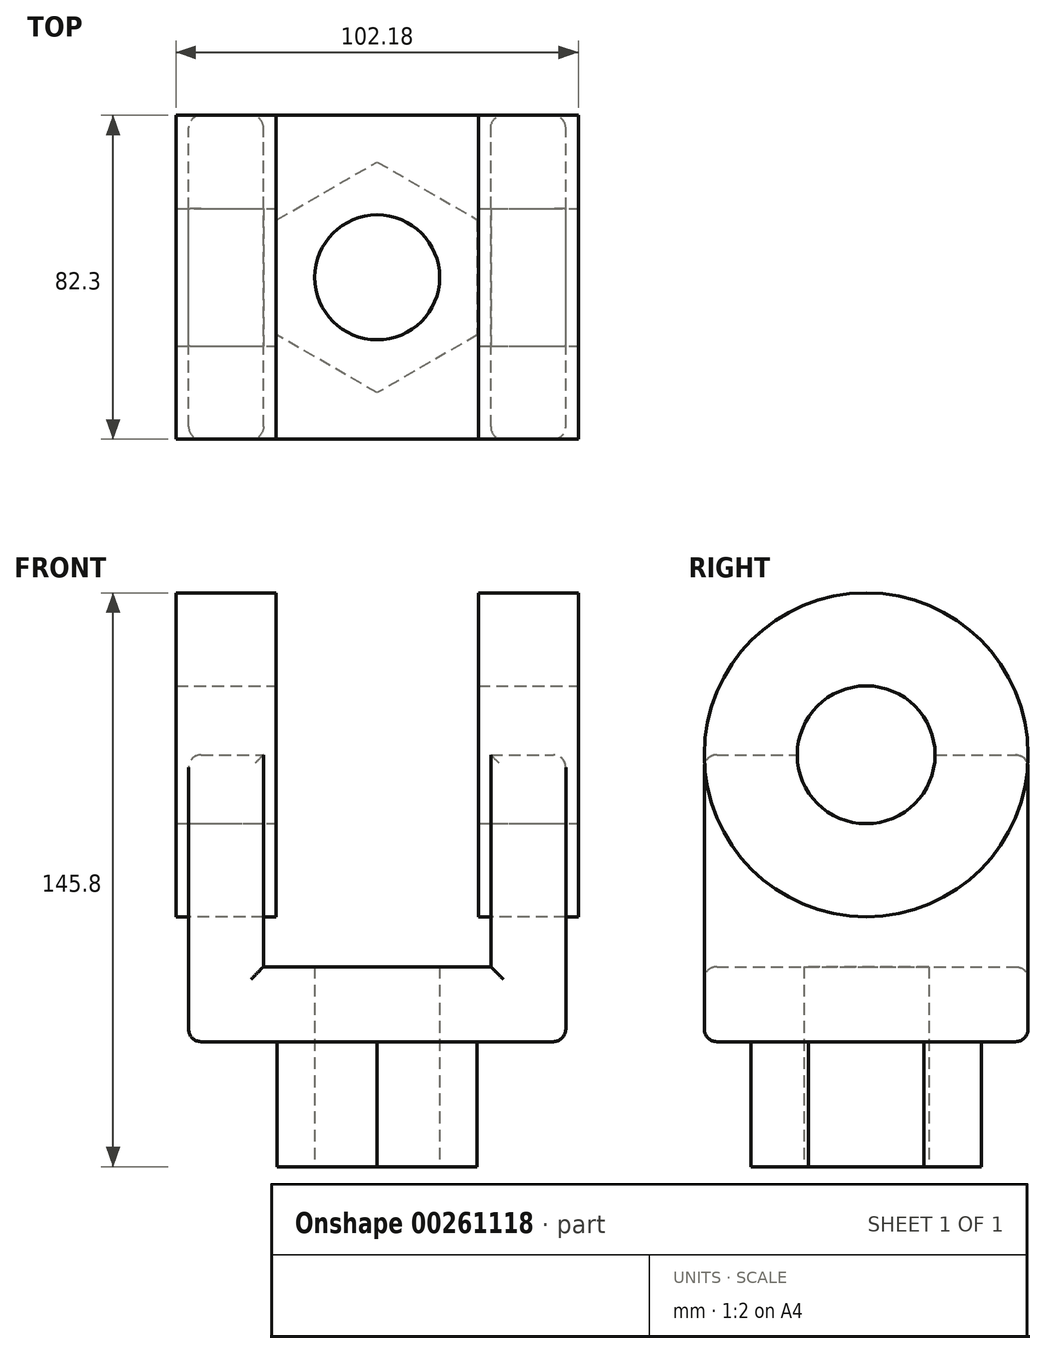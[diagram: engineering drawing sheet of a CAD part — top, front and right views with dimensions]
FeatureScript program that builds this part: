
annotation { "Feature Type Name" : "Feature", "Feature Type Description" : "" }
export const myFeature = defineFeature(function(context is Context, id is Id, definition is map)
    precondition{}
    {
        {
            var Q0;
            Q0=qCreatedBy(makeId("Right.planeOp"),FACE);
            var sketch = newSketch(context, id + "F0", { "sketchPlane" : qUnion([Q0])});
            skCircle(sketch, "E0", {"center": v(0, 0) * mm, "radius": 41.15 * mm});
            skSolve(sketch);
        }
        {
            var Q0;
            Q0 = qSketchRegion(id + "F0", true);
            extrude(context, id + "F1", {"entities" : qUnion([Q0]), "endBound" : BoundingType.SYMMETRIC, "depth" : 102.17 * mm});
        }
        {
            var Q0;
            Q0=qCreatedBy(makeId("Top.planeOp"),FACE);
            cPlane(context, id + "F2", {"entities" : qUnion([Q0]), "cplaneType" : CPlaneType.OFFSET, "offset" : 104.65 * mm, "oppositeDirection" : true, "width" : 152.4 * mm, "height" : 152.4 * mm});
        }
        {
            var Q0;
            Q0=qCreatedBy(id+"F2.planeOp",FACE);
            var sketch = newSketch(context, id + "F3", { "sketchPlane" : qUnion([Q0])});
            skCircle(sketch, "E1.cCircle", {"center": v(0, 0) * mm, "radius": 25.4 * mm, "construction": true});
            skLineSegment(sketch, "E1.0", {"start": v(-0.03, -29.33) * mm, "end": v(-25.41, -14.64) * mm});
            skLineSegment(sketch, "E1.1", {"start": v(-25.41, -14.64) * mm, "end": v(-25.39, 14.69) * mm});
            skLineSegment(sketch, "E1.2", {"start": v(-25.39, 14.69) * mm, "end": v(0.03, 29.33) * mm});
            skLineSegment(sketch, "E1.3", {"start": v(0.03, 29.33) * mm, "end": v(25.41, 14.64) * mm});
            skLineSegment(sketch, "E1.4", {"start": v(25.41, 14.64) * mm, "end": v(25.39, -14.69) * mm});
            skLineSegment(sketch, "E1.5", {"start": v(25.39, -14.69) * mm, "end": v(-0.03, -29.33) * mm});
            skPoint(sketch, "E1.0.midPoint", {"position": v(-12.72, -21.98) * mm});
            skSolve(sketch);
        }
        {
            var Q0;
            Q0=qCreatedBy(makeId("Front.planeOp"),FACE);
            var sketch = newSketch(context, id + "F4", { "sketchPlane" : qUnion([Q0])});
            skLineSegment(sketch, "E2.bottom", {"start": v(-25.69, -50.8) * mm, "end": v(25.69, -50.8) * mm});
            skLineSegment(sketch, "E2.top", {"start": v(-25.69, 50.8) * mm, "end": v(25.69, 50.8) * mm});
            skLineSegment(sketch, "E2.left", {"start": v(-25.69, -50.8) * mm, "end": v(-25.69, 50.8) * mm});
            skLineSegment(sketch, "E2.right", {"start": v(25.69, -50.8) * mm, "end": v(25.69, 50.8) * mm});
            skPoint(sketch, "E2.middle", {"position": v(0, 0) * mm});
            skSolve(sketch);
        }
        {
            var Q0;
            Q0 = qSketchRegion(id + "F4", true);
            extrude(context, id + "F5", {"entities" : qUnion([Q0]), "operationType" : NewBodyOperationType.REMOVE, "endBound" : BoundingType.SYMMETRIC, "oppositeDirection" : true, "depth" : 127 * mm});
        }
        {
            var Q0;
            Q0=qCreatedBy(makeId("Front.planeOp"),FACE);
            var sketch = newSketch(context, id + "F6", { "sketchPlane" : qUnion([Q0])});
            skLineSegment(sketch, "E3", {"start": v(-47.91, 0) * mm, "end": v(-47.91, -72.9) * mm});
            skLineSegment(sketch, "E4", {"start": v(-47.91, -72.9) * mm, "end": v(0, -72.9) * mm});
            skLineSegment(sketch, "E5", {"start": v(0, -72.9) * mm, "end": v(0, -53.85) * mm});
            skLineSegment(sketch, "E6", {"start": v(0, -53.85) * mm, "end": v(-28.86, -53.85) * mm});
            skLineSegment(sketch, "E7", {"start": v(-28.86, -53.85) * mm, "end": v(-28.86, 0) * mm});
            skLineSegment(sketch, "E8", {"start": v(-28.86, 0) * mm, "end": v(-47.91, 0) * mm});
            skLineSegment(sketch, "E9.MirrorCS", {"start": v(0, -53.85) * mm, "end": v(28.86, -53.85) * mm});
            skLineSegment(sketch, "E10.MirrorCS", {"start": v(47.91, -72.9) * mm, "end": v(0, -72.9) * mm});
            skLineSegment(sketch, "E11.MirrorCS", {"start": v(47.91, 0) * mm, "end": v(47.91, -72.9) * mm});
            skLineSegment(sketch, "E12.MirrorCS", {"start": v(28.86, -53.85) * mm, "end": v(28.86, 0) * mm});
            skLineSegment(sketch, "E13.MirrorCS", {"start": v(28.86, 0) * mm, "end": v(47.91, 0) * mm});
            skSolve(sketch);
        }
        {
            var Q0;
            Q0 = qSketchRegion(id + "F6", true);
            extrude(context, id + "F7", {"entities" : qUnion([Q0]), "endBound" : BoundingType.SYMMETRIC, "depth" : 82.3 * mm});
        }
        {
            var Q0;
            Q0=makeQuery(id+"F3.imprint","IMPRINT",FACE,{"disambiguationData":[TD([[makeQuery(id+"F3.imprint","IMPRINT",EDGE,{"derivedFrom":sQuery(id+"F3.wireOp",EDGE,"E1.0")}),-1.0]])]});
            extrude(context, id + "F8", {"entities" : qUnion([Q0]), "operationType" : NewBodyOperationType.ADD, "endBound" : BoundingType.UP_TO_NEXT, "depth" : 25.4 * mm});
        }
        {
            var Q0;
            Q0=makeQuery(id+"F7.opExtrude","SWEPT_FACE",FACE,{"disambiguationData":[OSD([sQuery(id+"F6.wireOp",EDGE,"E11.MirrorCS")])]});
            var Q1;
            Q1=makeQuery(id+"F7.opExtrude","SWEPT_FACE",FACE,{"disambiguationData":[OSD([sQuery(id+"F6.wireOp",EDGE,"E3")])]});
            var Q2;
            Q2=makeQuery(id+"F7.opExtrude","CAP_FACE",FACE,{"disambiguationData":[OSD([sQuery(id+"F6.wireOp",EDGE,"E3"),sQuery(id+"F6.wireOp",EDGE,"E4"),sQuery(id+"F6.wireOp",EDGE,"E6"),sQuery(id+"F6.wireOp",EDGE,"E7"),sQuery(id+"F6.wireOp",EDGE,"E8"),sQuery(id+"F6.wireOp",EDGE,"E9.MirrorCS"),sQuery(id+"F6.wireOp",EDGE,"E10.MirrorCS"),sQuery(id+"F6.wireOp",EDGE,"E11.MirrorCS"),sQuery(id+"F6.wireOp",EDGE,"E12.MirrorCS"),sQuery(id+"F6.wireOp",EDGE,"E13.MirrorCS")])],"isStart":false});
            var Q3;
            Q3=makeQuery(id+"F7.opExtrude","CAP_FACE",FACE,{"disambiguationData":[OSD([sQuery(id+"F6.wireOp",EDGE,"E3"),sQuery(id+"F6.wireOp",EDGE,"E4"),sQuery(id+"F6.wireOp",EDGE,"E6"),sQuery(id+"F6.wireOp",EDGE,"E7"),sQuery(id+"F6.wireOp",EDGE,"E8"),sQuery(id+"F6.wireOp",EDGE,"E9.MirrorCS"),sQuery(id+"F6.wireOp",EDGE,"E10.MirrorCS"),sQuery(id+"F6.wireOp",EDGE,"E11.MirrorCS"),sQuery(id+"F6.wireOp",EDGE,"E12.MirrorCS"),sQuery(id+"F6.wireOp",EDGE,"E13.MirrorCS")])],"isStart":true});
            fillet(context, id + "F9", {"entities" : qUnion([Q0, Q1, Q2, Q3]), "radius" : 3.17 * mm, "tangentPropagation" : true, "allowEdgeOverflow" : false});
        }
        {
            var Q0;
            Q0=qCreatedBy(makeId("Right.planeOp"),FACE);
            var sketch = newSketch(context, id + "F10", { "sketchPlane" : qUnion([Q0])});
            skCircle(sketch, "E14", {"center": v(0, 0) * mm, "radius": 17.5 * mm});
            skSolve(sketch);
        }
        {
            var Q0;
            Q0 = qSketchRegion(id + "F10", true);
            extrude(context, id + "F11", {"entities" : qUnion([Q0]), "operationType" : NewBodyOperationType.REMOVE, "endBound" : BoundingType.SYMMETRIC, "oppositeDirection" : true, "depth" : 127 * mm});
        }
        {
            var Q0;
            Q0=qCreatedBy(id+"F2.planeOp",FACE);
            var sketch = newSketch(context, id + "F12", { "sketchPlane" : qUnion([Q0])});
            skCircle(sketch, "E15", {"center": v(0, 0) * mm, "radius": 15.88 * mm});
            skSolve(sketch);
        }
        {
            var Q0;
            Q0 = qSketchRegion(id + "F12", true);
            extrude(context, id + "F13", {"entities" : qUnion([Q0]), "operationType" : NewBodyOperationType.REMOVE, "endBound" : BoundingType.UP_TO_NEXT, "depth" : 25.4 * mm});
        }
    });
